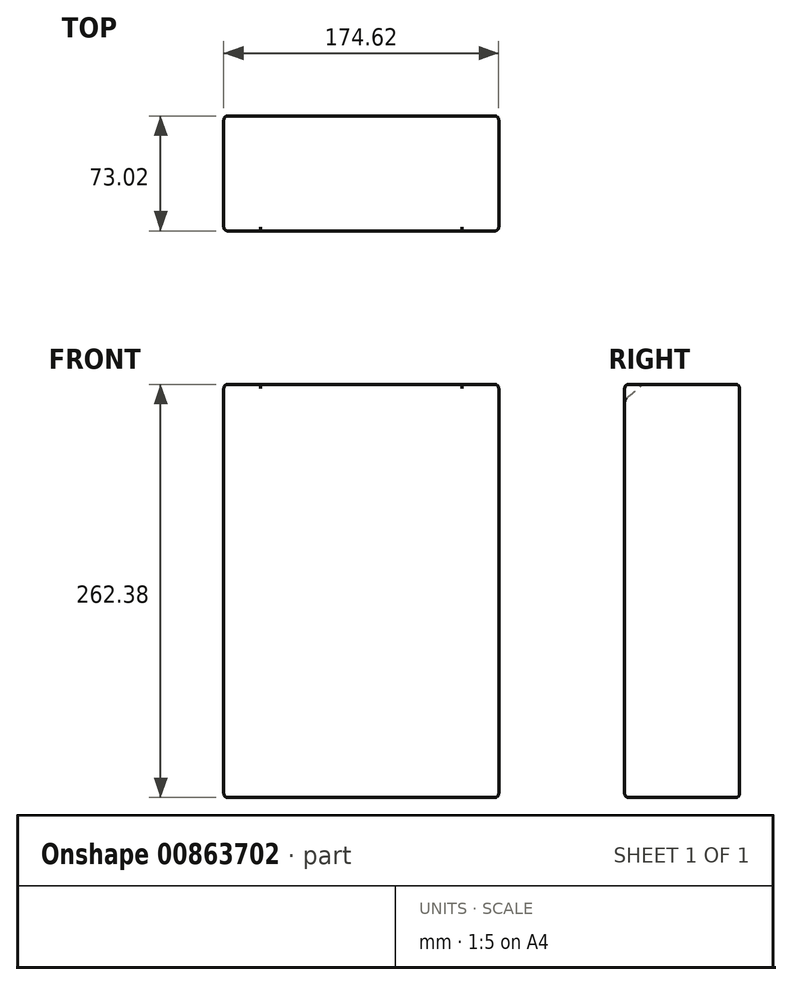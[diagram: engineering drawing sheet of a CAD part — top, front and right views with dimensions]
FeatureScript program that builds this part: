
annotation { "Feature Type Name" : "Feature", "Feature Type Description" : "" }
export const myFeature = defineFeature(function(context is Context, id is Id, definition is map)
    precondition{}
    {
        {
            var Q0;
            Q0=qCreatedBy(makeId("Top.planeOp"),FACE);
            var sketch = newSketch(context, id + "F0", { "sketchPlane" : qUnion([Q0])});
            skLineSegment(sketch, "E0.bottom", {"start": v(-87.31, 36.51) * mm, "end": v(87.31, 36.51) * mm});
            skLineSegment(sketch, "E0.top", {"start": v(-87.31, -36.51) * mm, "end": v(87.31, -36.51) * mm});
            skLineSegment(sketch, "E0.left", {"start": v(-87.31, 36.51) * mm, "end": v(-87.31, -36.51) * mm});
            skLineSegment(sketch, "E0.right", {"start": v(87.31, 36.51) * mm, "end": v(87.31, -36.51) * mm});
            skPoint(sketch, "E0.middle", {"position": v(0, 0) * mm});
            skSolve(sketch);
        }
        {
            var Q0;
            Q0=makeQuery(id+"F0.imprint","IMPRINT",FACE,{"disambiguationData":[TD([[makeQuery(id+"F0.imprint","IMPRINT",EDGE,{"derivedFrom":sQuery(id+"F0.wireOp",EDGE,"E0.bottom")}),-1.0]])]});
            extrude(context, id + "F1", {"entities" : qUnion([Q0]), "depth" : 262.38 * mm, "offsetDistance" : 25.4 * mm});
        }
        {
            var Q0;
            Q0=qCreatedBy(makeId("Top.planeOp"),FACE);
            cPlane(context, id + "F2", {"entities" : qUnion([Q0]), "cplaneType" : CPlaneType.OFFSET, "offset" : 497.33 * mm, "width" : 152.4 * mm, "height" : 152.4 * mm});
        }
        {
            var Q0;
            Q0=qCreatedBy(id+"F2.planeOp",FACE);
            var sketch = newSketch(context, id + "F3", { "sketchPlane" : qUnion([Q0])});
            skArc(sketch, "E1", {"start": v(317.5, -238.76) * mm, "mid": v(0, 78.74) * mm, "end": v(-317.5, -238.76) * mm});
            skLineSegment(sketch, "E2", {"start": v(0, -238.76) * mm, "end": v(-317.5, -238.76) * mm});
            skLineSegment(sketch, "E3", {"start": v(0, -238.76) * mm, "end": v(317.5, -238.76) * mm});
            skLineSegment(sketch, "E4", {"start": v(-317.5, -238.76) * mm, "end": v(-369.58, -238.76) * mm});
            skSolve(sketch);
        }
        {
            var Q0;
            Q0=makeQuery(id+"F3.imprint","IMPRINT",FACE,{"disambiguationData":[TD([[makeQuery(id+"F3.imprint","IMPRINT",EDGE,{"derivedFrom":sQuery(id+"F3.wireOp",EDGE,"E1")}),1.0]])]});
            var Q1;
            Q1=sQuery(id+"F3.wireOp",EDGE,"E4");
            revolve(context, id + "F4", {"operationType" : NewBodyOperationType.REMOVE, "surfaceOperationType" : NewSurfaceOperationType.NEW, "entities" : qUnion([Q0]), "axis" : qUnion([Q1]), "revolveType" : RevolveType.FULL});
        }
        {
            var Q0;
            Q0=makeQuery(id+"F4.boolean.opBoolean","INTERSECT",EDGE,{"derivedFrom":[makeQuery(id+"F1.opExtrude","SWEPT_FACE",FACE,{"disambiguationData":[OSD([sQuery(id+"F0.wireOp",EDGE,"E0.top")])]}),makeQuery(id+"F4.opRevolve","SWEPT_FACE",FACE,{"disambiguationData":[OSD([sQuery(id+"F3.wireOp",EDGE,"E1")])]})]});
            var Q1;
            Q1=makeQuery(id+"F4.boolean.opBoolean","INTERSECT",EDGE,{"derivedFrom":[makeQuery(id+"F1.opExtrude","CAP_FACE",FACE,{"disambiguationData":[OSD([sQuery(id+"F0.wireOp",EDGE,"E0.bottom"),sQuery(id+"F0.wireOp",EDGE,"E0.top"),sQuery(id+"F0.wireOp",EDGE,"E0.left"),sQuery(id+"F0.wireOp",EDGE,"E0.right")])],"isStart":false}),makeQuery(id+"F4.opRevolve","SWEPT_FACE",FACE,{"disambiguationData":[OSD([sQuery(id+"F3.wireOp",EDGE,"E1")])]})]});
            var Q2;
            {var subQ0=sQuery(id+"F0.wireOp",EDGE,"E0.left");var subQ1=sQuery(id+"F0.wireOp",EDGE,"E0.top");Q2=makeQuery(id+"F4.boolean.opBoolean","SPLIT",EDGE,{"disambiguationData":[TD([makeQuery(id+"F1.opExtrude","SWEPT_FACE",FACE,{"disambiguationData":[OSD([subQ0])]})])],"derivedFrom":makeQuery(id+"F1.opExtrude","CAP_EDGE",EDGE,{"disambiguationData":[OSD([subQ1])],"isStart":false})});}
            var Q3;
            {var subQ0=sQuery(id+"F0.wireOp",EDGE,"E0.right");var subQ1=sQuery(id+"F0.wireOp",EDGE,"E0.top");Q3=makeQuery(id+"F4.boolean.opBoolean","SPLIT",EDGE,{"disambiguationData":[TD([makeQuery(id+"F1.opExtrude","SWEPT_FACE",FACE,{"disambiguationData":[OSD([subQ0])]})])],"derivedFrom":makeQuery(id+"F1.opExtrude","CAP_EDGE",EDGE,{"disambiguationData":[OSD([subQ1])],"isStart":false})});}
            var Q4;
            Q4=makeQuery(id+"F1.opExtrude","SWEPT_EDGE",EDGE,{"disambiguationData":[OSD([sQuery(id+"F0.wireOp",EDGE,"E0.top"),sQuery(id+"F0.wireOp",EDGE,"E0.right")])]});
            var Q5;
            Q5=makeQuery(id+"F1.opExtrude","CAP_EDGE",EDGE,{"disambiguationData":[OSD([sQuery(id+"F0.wireOp",EDGE,"E0.right")])],"isStart":false});
            var Q6;
            Q6=makeQuery(id+"F1.opExtrude","SWEPT_EDGE",EDGE,{"disambiguationData":[OSD([sQuery(id+"F0.wireOp",EDGE,"E0.bottom"),sQuery(id+"F0.wireOp",EDGE,"E0.right")])]});
            var Q7;
            Q7=makeQuery(id+"F1.opExtrude","CAP_EDGE",EDGE,{"disambiguationData":[OSD([sQuery(id+"F0.wireOp",EDGE,"E0.bottom")])],"isStart":false});
            var Q8;
            Q8=makeQuery(id+"F1.opExtrude","CAP_EDGE",EDGE,{"disambiguationData":[OSD([sQuery(id+"F0.wireOp",EDGE,"E0.left")])],"isStart":false});
            var Q9;
            Q9=makeQuery(id+"F1.opExtrude","SWEPT_EDGE",EDGE,{"disambiguationData":[OSD([sQuery(id+"F0.wireOp",EDGE,"E0.top"),sQuery(id+"F0.wireOp",EDGE,"E0.left")])]});
            var Q10;
            Q10=makeQuery(id+"F1.opExtrude","CAP_EDGE",EDGE,{"disambiguationData":[OSD([sQuery(id+"F0.wireOp",EDGE,"E0.top")])],"isStart":true});
            var Q11;
            Q11=makeQuery(id+"F1.opExtrude","CAP_EDGE",EDGE,{"disambiguationData":[OSD([sQuery(id+"F0.wireOp",EDGE,"E0.right")])],"isStart":true});
            var Q12;
            Q12=makeQuery(id+"F1.opExtrude","CAP_EDGE",EDGE,{"disambiguationData":[OSD([sQuery(id+"F0.wireOp",EDGE,"E0.bottom")])],"isStart":true});
            var Q13;
            Q13=makeQuery(id+"F1.opExtrude","CAP_EDGE",EDGE,{"disambiguationData":[OSD([sQuery(id+"F0.wireOp",EDGE,"E0.left")])],"isStart":true});
            var Q14;
            Q14=makeQuery(id+"F1.opExtrude","SWEPT_EDGE",EDGE,{"disambiguationData":[OSD([sQuery(id+"F0.wireOp",EDGE,"E0.bottom"),sQuery(id+"F0.wireOp",EDGE,"E0.left")])]});
            fillet(context, id + "F5", {"entities" : qUnion([Q0, Q1, Q2, Q3, Q4, Q5, Q6, Q7, Q8, Q9, Q10, Q11, Q12, Q13, Q14]), "radius" : 2.54 * mm, "tangentPropagation" : true, "allowEdgeOverflow" : false});
        }
    });
